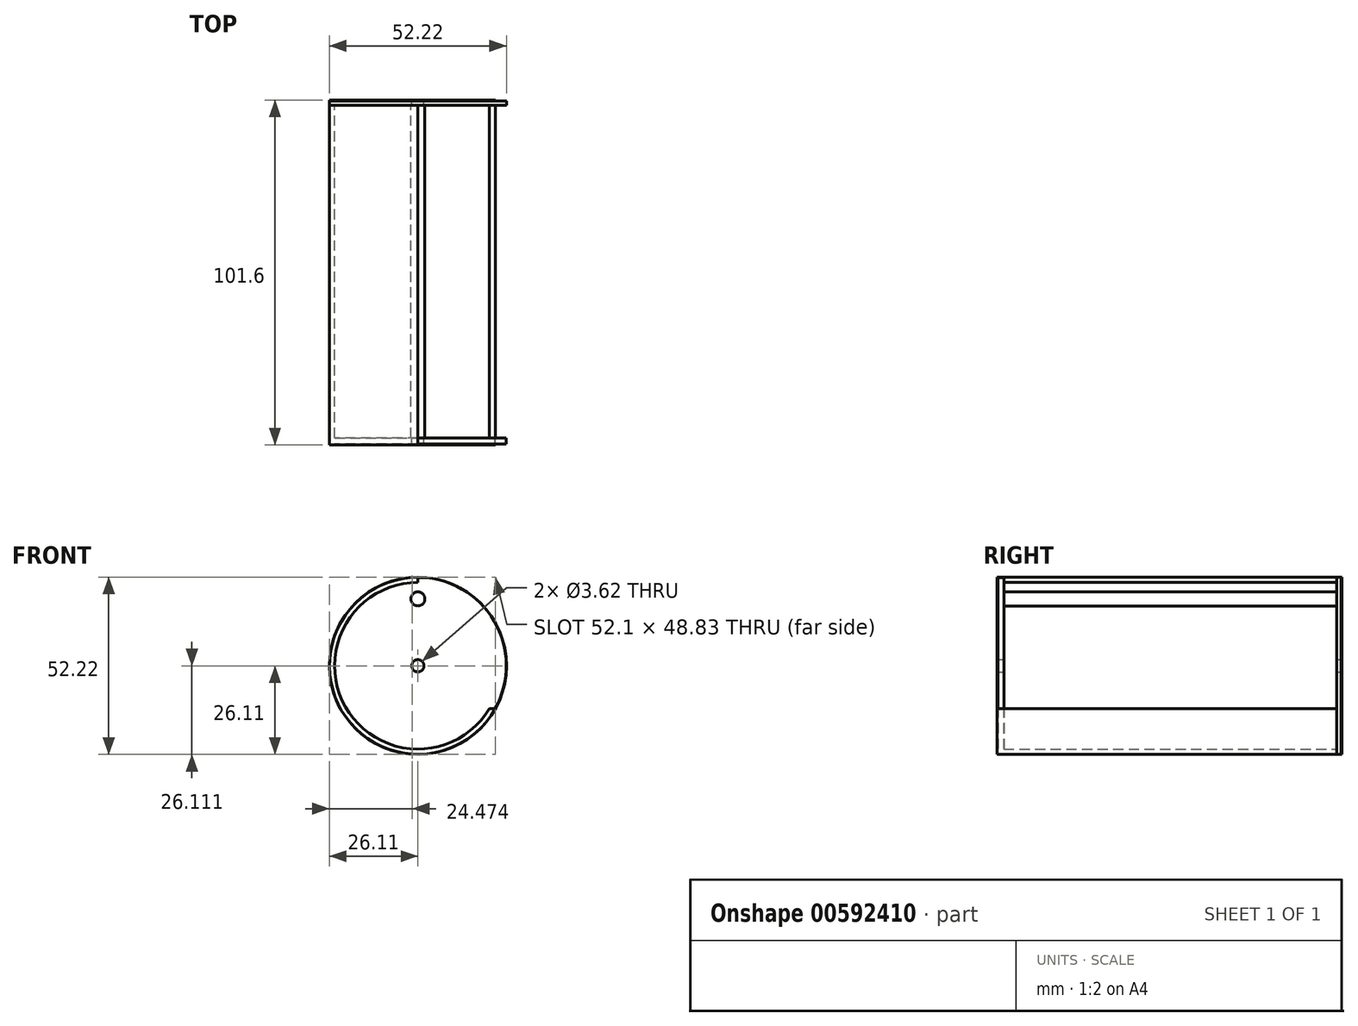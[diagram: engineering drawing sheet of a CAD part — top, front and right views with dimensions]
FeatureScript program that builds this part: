
annotation { "Feature Type Name" : "Feature", "Feature Type Description" : "" }
export const myFeature = defineFeature(function(context is Context, id is Id, definition is map)
    precondition{}
    {
        {
            var Q0;
            Q0=qCreatedBy(makeId("Front.planeOp"),FACE);
            var sketch = newSketch(context, id + "F0", { "sketchPlane" : qUnion([Q0])});
            skCircle(sketch, "E0", {"center": v(0, 0) * mm, "radius": 26.05 * mm});
            skCircle(sketch, "E1", {"center": v(0, 0) * mm, "radius": 24.54 * mm});
            skSolve(sketch);
        }
        {
            var Q0;
            Q0 = qSketchRegion(id + "F0", true);
            extrude(context, id + "F1", {"entities" : qUnion([Q0]), "endBound" : BoundingType.SYMMETRIC, "depth" : 101.6 * mm, "offsetDistance" : 25.4 * mm});
        }
        {
            var Q0;
            Q0=qCreatedBy(makeId("Front.planeOp"),FACE);
            var sketch = newSketch(context, id + "F2", { "sketchPlane" : qUnion([Q0])});
            skLineSegment(sketch, "E2", {"start": v(0, 35.4) * mm, "end": v(0, -12.64) * mm});
            skLineSegment(sketch, "E3", {"start": v(0, -12.64) * mm, "end": v(37.8, -12.64) * mm});
            skLineSegment(sketch, "E4", {"start": v(37.8, -12.64) * mm, "end": v(37.8, 35.4) * mm});
            skLineSegment(sketch, "E5", {"start": v(37.8, 35.4) * mm, "end": v(0, 35.4) * mm});
            skSolve(sketch);
        }
        {
            var Q0;
            Q0=makeQuery(id+"F2.imprint","IMPRINT",FACE,{"disambiguationData":[TD([[makeQuery(id+"F2.imprint","IMPRINT",EDGE,{"derivedFrom":sQuery(id+"F2.wireOp",EDGE,"E2")}),1.0]])]});
            extrude(context, id + "F3", {"entities" : qUnion([Q0]), "operationType" : NewBodyOperationType.REMOVE, "endBound" : BoundingType.SYMMETRIC, "oppositeDirection" : true, "depth" : 101.6 * mm, "offsetDistance" : 25.4 * mm});
        }
        {
            var Q0;
            Q0=qCreatedBy(makeId("Front.planeOp"),FACE);
            var sketch = newSketch(context, id + "F4", { "sketchPlane" : qUnion([Q0])});
            skLineSegment(sketch, "E6", {"start": v(21.87, -12.13) * mm, "end": v(-21.1, -12.13) * mm});
            skSolve(sketch);
        }
        {
            var Q0;
            Q0=sQuery(id+"F4.wireOp",EDGE,"E6");
            extrude(context, id + "F5", {"bodyType" : ToolBodyType.SURFACE, "surfaceEntities" : qUnion([Q0]), "endBound" : BoundingType.SYMMETRIC, "depth" : 101.6 * mm, "offsetDistance" : 25.4 * mm});
        }
        {
            var Q0;
            Q0=qCreatedBy(makeId("Front.planeOp"),FACE);
            var sketch = newSketch(context, id + "F6", { "sketchPlane" : qUnion([Q0])});
            skCircle(sketch, "E7", {"center": v(0, 0) * mm, "radius": 26.04 * mm});
            skSolve(sketch);
        }
        {
            var Q0;
            Q0 = qSketchRegion(id + "F6", true);
            extrude(context, id + "F7", {"entities" : qUnion([Q0]), "operationType" : NewBodyOperationType.ADD, "depth" : 50.55 * mm, "offsetDistance" : 25.4 * mm, "hasSecondDirection" : true, "secondDirectionOppositeDirection" : false, "secondDirectionDepth" : 48.77 * mm});
        }
        {
            var Q0;
            Q0=qCreatedBy(makeId("Front.planeOp"),FACE);
            var sketch = newSketch(context, id + "F8", { "sketchPlane" : qUnion([Q0])});
            skCircle(sketch, "E8", {"center": v(0, 0) * mm, "radius": 26.1 * mm});
            skSolve(sketch);
        }
        {
            var Q0;
            Q0 = qSketchRegion(id + "F8", true);
            extrude(context, id + "F9", {"entities" : qUnion([Q0]), "operationType" : NewBodyOperationType.ADD, "oppositeDirection" : true, "depth" : 50.55 * mm, "offsetDistance" : 25.4 * mm, "hasSecondDirection" : true, "secondDirectionOppositeDirection" : true, "secondDirectionDepth" : 49.28 * mm});
        }
        {
            var Q0;
            Q0=qCreatedBy(makeId("Front.planeOp"),FACE);
            var sketch = newSketch(context, id + "F10", { "sketchPlane" : qUnion([Q0])});
            skCircle(sketch, "E9", {"center": v(0, 19.72) * mm, "radius": 2.06 * mm});
            skSolve(sketch);
        }
        {
            var Q0;
            Q0 = qSketchRegion(id + "F10", true);
            extrude(context, id + "F11", {"entities" : qUnion([Q0]), "operationType" : NewBodyOperationType.ADD, "endBound" : BoundingType.SYMMETRIC, "depth" : 101.6 * mm, "offsetDistance" : 25.4 * mm});
        }
        {
            var Q0;
            Q0=qCreatedBy(makeId("Front.planeOp"),FACE);
            var sketch = newSketch(context, id + "F12", { "sketchPlane" : qUnion([Q0])});
            skCircle(sketch, "E10", {"center": v(0, 0) * mm, "radius": 1.8 * mm});
            skSolve(sketch);
        }
        {
            var Q0;
            Q0 = qSketchRegion(id + "F12", true);
            extrude(context, id + "F13", {"entities" : qUnion([Q0]), "operationType" : NewBodyOperationType.REMOVE, "endBound" : BoundingType.SYMMETRIC, "depth" : 101.6 * mm, "offsetDistance" : 25.4 * mm});
        }
    });
